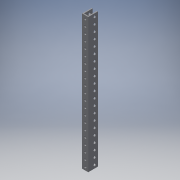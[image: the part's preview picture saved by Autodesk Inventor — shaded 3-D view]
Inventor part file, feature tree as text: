
AUTODESK INVENTOR PART (.ipt)
format: ipt  version: 2017 (Build 210142000, 142)  size: 168,448 bytes
history: native  units: in
note: dims shown in document units (in); Inventor stores cm internally (conversion verified against a paired STEP export)
features: fillet x1
ambient origin geometry x8: Origin, YZ Plane, XZ Plane, XY Plane, X Axis, Y Axis, Z Axis, Center Point
bodies: Solid1 (feature_tree)
feature tree (1):
  fillet  "Fillet1"  [1 undecoded]
note: 1 required parameter value undecoded (feature->parameter linkage not recoverable at this tier; creation-order binding heuristic only, values carry confidence <= 0.55)
